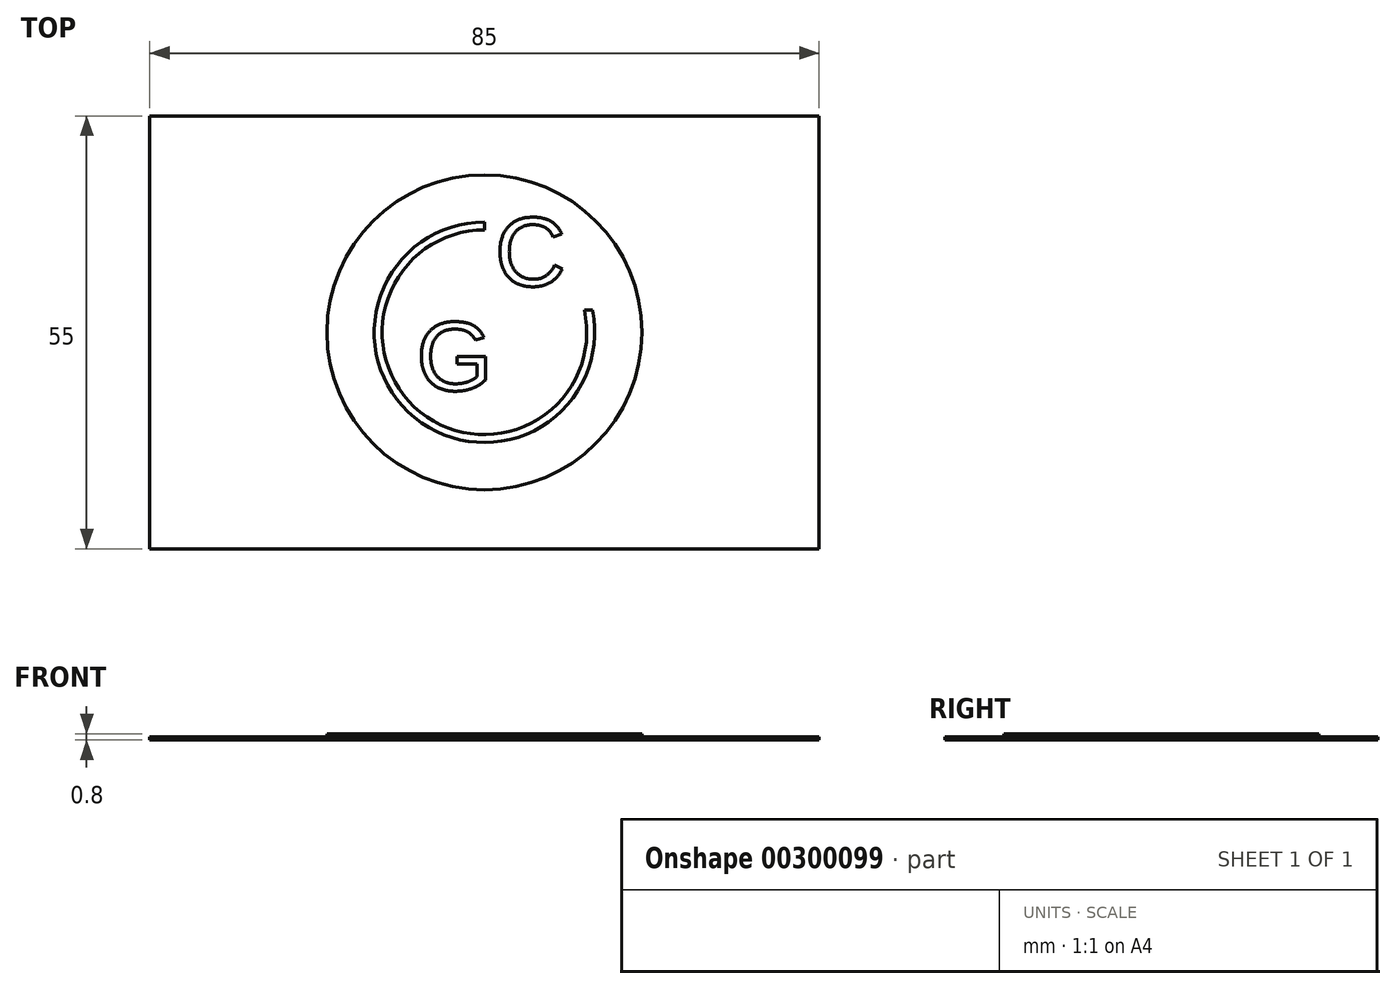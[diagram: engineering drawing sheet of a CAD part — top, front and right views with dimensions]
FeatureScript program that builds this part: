
annotation { "Feature Type Name" : "Feature", "Feature Type Description" : "" }
export const myFeature = defineFeature(function(context is Context, id is Id, definition is map)
    precondition{}
    {
        {
            var Q0;
            Q0=qCreatedBy(makeId("Top.planeOp"),FACE);
            var sketch = newSketch(context, id + "F0", { "sketchPlane" : qUnion([Q0])});
            skLineSegment(sketch, "E0.bottom", {"start": v(-42.5, 27.5) * mm, "end": v(42.5, 27.5) * mm});
            skLineSegment(sketch, "E0.top", {"start": v(-42.5, -27.5) * mm, "end": v(42.5, -27.5) * mm});
            skLineSegment(sketch, "E0.left", {"start": v(-42.5, 27.5) * mm, "end": v(-42.5, -27.5) * mm});
            skLineSegment(sketch, "E0.right", {"start": v(42.5, 27.5) * mm, "end": v(42.5, -27.5) * mm});
            skSolve(sketch);
        }
        {
            var Q0;
            Q0=makeQuery(id+"F0.imprint","IMPRINT",FACE,{"disambiguationData":[TD([[makeQuery(id+"F0.imprint","IMPRINT",EDGE,{"derivedFrom":sQuery(id+"F0.wireOp",EDGE,"E0.bottom")}),-1.0]])]});
            extrude(context, id + "F1", {"entities" : qUnion([Q0]), "depth" : 0.4 * mm});
        }
        {
            var Q0;
            Q0=makeQuery(id+"F1.opExtrude","CAP_FACE",FACE,{"disambiguationData":[OSD([sQuery(id+"F0.wireOp",EDGE,"E0.bottom"),sQuery(id+"F0.wireOp",EDGE,"E0.top"),sQuery(id+"F0.wireOp",EDGE,"E0.left"),sQuery(id+"F0.wireOp",EDGE,"E0.right")])],"isStart":false});
            var sketch = newSketch(context, id + "F2", { "sketchPlane" : qUnion([Q0])});
            skCircle(sketch, "E1", {"center": v(0, 0) * mm, "radius": 20 * mm});
            skArc(sketch, "E2", {"start": v(0, 14) * mm, "mid": v(-8.85, -10.85) * mm, "end": v(13.72, 2.8) * mm});
            skArc(sketch, "E3", {"start": v(0, 13) * mm, "mid": v(-8.14, -10.14) * mm, "end": v(12.7, 2.8) * mm});
            skLineSegment(sketch, "E4", {"start": v(0, 13) * mm, "end": v(0, 14) * mm});
            skLineSegment(sketch, "E5", {"start": v(12.7, 2.8) * mm, "end": v(13.72, 2.8) * mm});
            skText(sketch, "E6", { "text": "C", "fontName": "Arimo-Regular.ttf"});
            skText(sketch, "E7", { "text": "G", "fontName": "Arimo-Regular.ttf"});
            const initialGuessF2  = {"E6": [0.00134, 0.0059, 1, 0, 0.009], "E7": [-0.00864, -0.00737, 1, 0, 0.009]};
            skSetInitialGuess(sketch, initialGuessF2);
            skSolve(sketch);
        }
        {
            var Q0;
            Q0 = qSketchRegion(id + "F2", true);
            extrude(context, id + "F3", {"entities" : qUnion([Q0]), "operationType" : NewBodyOperationType.ADD, "depth" : 0.4 * mm});
        }
    });
